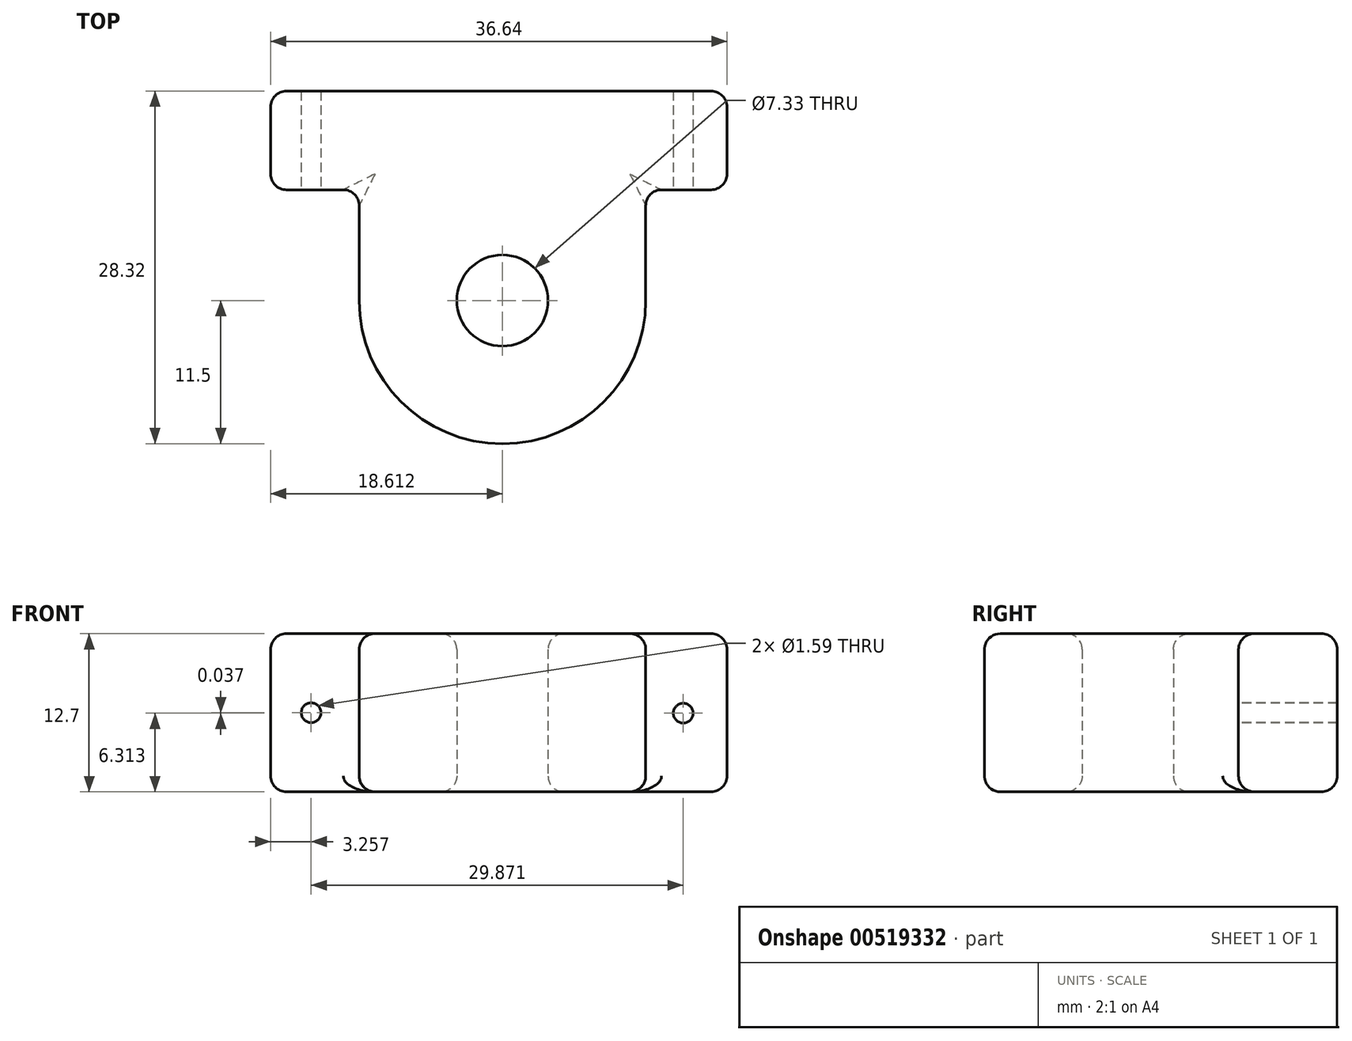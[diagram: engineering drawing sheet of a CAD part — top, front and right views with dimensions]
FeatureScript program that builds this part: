
annotation { "Feature Type Name" : "Feature", "Feature Type Description" : "" }
export const myFeature = defineFeature(function(context is Context, id is Id, definition is map)
    precondition{}
    {
        {
            var Q0;
            Q0=qCreatedBy(makeId("Top.planeOp"),FACE);
            var sketch = newSketch(context, id + "F0", { "sketchPlane" : qUnion([Q0])});
            skLineSegment(sketch, "E0.bottom", {"start": v(-36.64, 0) * mm, "end": v(0, 0) * mm});
            skLineSegment(sketch, "E0.top", {"start": v(-36.64, 7.93) * mm, "end": v(0, 7.93) * mm});
            skLineSegment(sketch, "E0.left", {"start": v(-36.64, 0) * mm, "end": v(-36.64, 7.93) * mm});
            skLineSegment(sketch, "E0.right", {"start": v(0, 0) * mm, "end": v(0, 7.93) * mm});
            skLineSegment(sketch, "E1", {"start": v(-29.53, 0) * mm, "end": v(-29.53, -8.9) * mm});
            skLineSegment(sketch, "E2", {"start": v(-6.52, 0) * mm, "end": v(-6.52, -8.9) * mm});
            skArc(sketch, "E3", {"start": v(-29.53, -8.9) * mm, "mid": v(-18.03, -20.4) * mm, "end": v(-6.52, -8.9) * mm});
            skCircle(sketch, "E4", {"center": v(-18.03, -8.9) * mm, "radius": 3.66 * mm});
            skSolve(sketch);
        }
        {
            var Q0;
            {var subQ1=sQuery(id+"F0.wireOp",EDGE,"E1");Q0=makeQuery(id+"F0.imprint","IMPRINT",FACE,{"disambiguationData":[TD([[makeQuery(id+"F0.imprint","IMPRINT",EDGE,{"derivedFrom":subQ1}),1.0]])]});}
            var Q1;
            Q1=makeQuery(id+"F0.imprint","IMPRINT",FACE,{"disambiguationData":[TD([[makeQuery(id+"F0.imprint","IMPRINT",EDGE,{"derivedFrom":sQuery(id+"F0.wireOp",EDGE,"E0.top")}),-1.0]])]});
            extrude(context, id + "F1", {"entities" : qUnion([Q0, Q1]), "depth" : 12.7 * mm, "offsetDistance" : 25.4 * mm});
        }
        {
            var Q0;
            Q0=makeQuery(id+"F1.opExtrude","SWEPT_FACE",FACE,{"disambiguationData":[OSD([sQuery(id+"F0.wireOp",EDGE,"E0.left")])]});
            var Q1;
            Q1=makeQuery(id+"F1.opExtrude","CAP_FACE",FACE,{"disambiguationData":[OSD([sQuery(id+"F0.wireOp",EDGE,"E0.bottom"),sQuery(id+"F0.wireOp",EDGE,"E0.top"),sQuery(id+"F0.wireOp",EDGE,"E0.left"),sQuery(id+"F0.wireOp",EDGE,"E0.right"),sQuery(id+"F0.wireOp",EDGE,"E1"),sQuery(id+"F0.wireOp",EDGE,"E2"),sQuery(id+"F0.wireOp",EDGE,"E3"),sQuery(id+"F0.wireOp",EDGE,"E4")])],"isStart":true});
            var Q2;
            Q2=makeQuery(id+"F1.opExtrude","SWEPT_FACE",FACE,{"disambiguationData":[OSD([sQuery(id+"F0.wireOp",EDGE,"E0.top")])]});
            fillet(context, id + "F2", {"entities" : qUnion([Q0, Q1, Q2]), "radius" : 1.27 * mm, "tangentPropagation" : true, "allowEdgeOverflow" : false});
        }
        {
            var Q0;
            Q0=makeQuery(id+"F1.opExtrude","SWEPT_FACE",FACE,{"disambiguationData":[OSD([sQuery(id+"F0.wireOp",EDGE,"E3")])]});
            var Q1;
            Q1=makeQuery(id+"F1.opExtrude","SWEPT_FACE",FACE,{"disambiguationData":[OSD([sQuery(id+"F0.wireOp",EDGE,"E2")])]});
            var Q2;
            Q2=makeQuery(id+"F1.opExtrude","SWEPT_FACE",FACE,{"disambiguationData":[OSD([sQuery(id+"F0.wireOp",EDGE,"E0.right")])]});
            var Q3;
            {var subQ0=sQuery(id+"F0.wireOp",EDGE,"E0.bottom");Q3=makeQuery(id+"F1.opExtrude","SWEPT_FACE",FACE,{"disambiguationData":[OSD([subQ0]),TDD([makeQuery(id+"F0.imprint","IMPRINT",EDGE,{"disambiguationData":[TD([[makeQuery(id+"F0.imprint","INTERSECT",VERTEX,{"derivedFrom":[subQ0,sQuery(id+"F0.wireOp",EDGE,"E0.right")]}),1.0]])],"derivedFrom":subQ0})])]});}
            var Q4;
            Q4=makeQuery(id+"F1.opExtrude","CAP_FACE",FACE,{"disambiguationData":[OSD([sQuery(id+"F0.wireOp",EDGE,"E0.bottom"),sQuery(id+"F0.wireOp",EDGE,"E0.top"),sQuery(id+"F0.wireOp",EDGE,"E0.left"),sQuery(id+"F0.wireOp",EDGE,"E0.right"),sQuery(id+"F0.wireOp",EDGE,"E1"),sQuery(id+"F0.wireOp",EDGE,"E2"),sQuery(id+"F0.wireOp",EDGE,"E3"),sQuery(id+"F0.wireOp",EDGE,"E4")])],"isStart":false});
            var Q5;
            Q5=makeQuery(id+"F1.opExtrude","SWEPT_EDGE",EDGE,{"disambiguationData":[OSD([sQuery(id+"F0.wireOp",EDGE,"E0.bottom"),sQuery(id+"F0.wireOp",EDGE,"E0.right")])]});
            var Q6;
            Q6=makeQuery(id+"F1.opExtrude","SWEPT_FACE",FACE,{"disambiguationData":[OSD([sQuery(id+"F0.wireOp",EDGE,"E1")])]});
            fillet(context, id + "F3", {"entities" : qUnion([Q0, Q1, Q2, Q3, Q4, Q5, Q6]), "radius" : 1.27 * mm, "tangentPropagation" : true, "allowEdgeOverflow" : false});
        }
        {
            var Q0;
            {var subQ0=sQuery(id+"F0.wireOp",EDGE,"E0.bottom");Q0=makeQuery(id+"F1.opExtrude","SWEPT_FACE",FACE,{"disambiguationData":[OSD([subQ0]),TDD([makeQuery(id+"F0.imprint","IMPRINT",EDGE,{"disambiguationData":[TD([[makeQuery(id+"F0.imprint","INTERSECT",VERTEX,{"derivedFrom":[subQ0,sQuery(id+"F0.wireOp",EDGE,"E0.right")]}),1.0]])],"derivedFrom":subQ0})])]});}
            var sketch = newSketch(context, id + "F4", { "sketchPlane" : qUnion([Q0])});
            skPoint(sketch, "E5", {"position": v(-3.51, 6.31) * mm});
            skPoint(sketch, "E6", {"position": v(-33.38, 6.35) * mm});
            skPoint(sketch, "E6.positionSnap0", {"position": v(-5.25, 6.35) * mm});
            skSolve(sketch);
        }
        {
            var Q0;
            Q0=sQuery(id+"F4.wireOp",VERTEX,"E5");
            var Q1;
            Q1=sQuery(id+"F4.wireOp",VERTEX,"E6");
            var Q2;
            Q2=makeQuery(id+"F1.opExtrude","SWEPT_BODY",BODY,{"disambiguationData":[OSD([sQuery(id+"F0.wireOp",EDGE,"E0.bottom"),sQuery(id+"F0.wireOp",EDGE,"E0.top"),sQuery(id+"F0.wireOp",EDGE,"E0.left"),sQuery(id+"F0.wireOp",EDGE,"E0.right"),sQuery(id+"F0.wireOp",EDGE,"E1"),sQuery(id+"F0.wireOp",EDGE,"E2"),sQuery(id+"F0.wireOp",EDGE,"E3"),sQuery(id+"F0.wireOp",EDGE,"E4")])]});
            hole(context, id + "F5", {"style" : HoleStyle.SIMPLE, "endStyle" : HoleEndStyle.THROUGH, "holeDiameter" : 1.59 * mm, "isTappedThrough" : true, "tappedDepth" : 12.7 * mm, "tapClearance" : 3, "locations" : qUnion([Q0, Q1]), "scope" : qUnion([Q2])});
        }
    });
